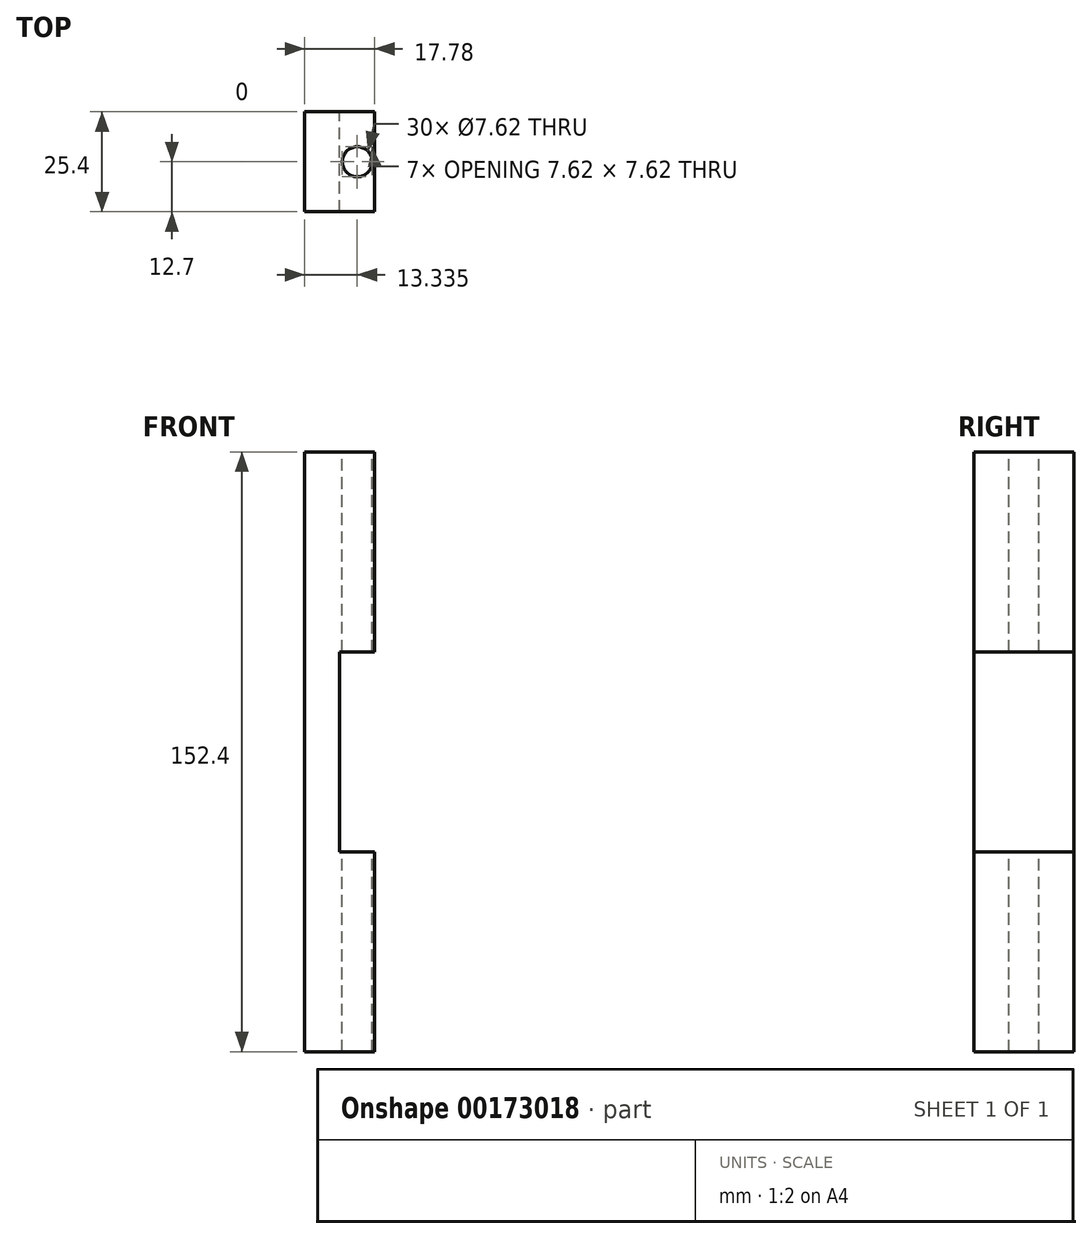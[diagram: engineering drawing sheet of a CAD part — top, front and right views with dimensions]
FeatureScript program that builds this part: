
annotation { "Feature Type Name" : "Feature", "Feature Type Description" : "" }
export const myFeature = defineFeature(function(context is Context, id is Id, definition is map)
    precondition{}
    {
        {
            var Q0;
            Q0=qCreatedBy(makeId("Front.planeOp"),FACE);
            var sketch = newSketch(context, id + "F0", { "sketchPlane" : qUnion([Q0])});
            skLineSegment(sketch, "E0.bottom", {"start": v(8.89, -76.2) * mm, "end": v(-8.9, -76.2) * mm});
            skLineSegment(sketch, "E0.top", {"start": v(8.9, 76.2) * mm, "end": v(-8.89, 76.2) * mm});
            skLineSegment(sketch, "E0.right", {"start": v(-8.9, -76.2) * mm, "end": v(-8.89, 76.2) * mm});
            skPoint(sketch, "E0.middle", {"position": v(0, 0) * mm});
            skLineSegment(sketch, "E1", {"start": v(8.9, 76.2) * mm, "end": v(8.9, 25.4) * mm});
            skLineSegment(sketch, "E2", {"start": v(8.9, 25.4) * mm, "end": v(0, 25.4) * mm});
            skLineSegment(sketch, "E3", {"start": v(8.89, -76.2) * mm, "end": v(8.89, -25.4) * mm});
            skLineSegment(sketch, "E4", {"start": v(8.89, -25.4) * mm, "end": v(0, -25.4) * mm});
            skLineSegment(sketch, "E5", {"start": v(0, -25.4) * mm, "end": v(0, 25.4) * mm});
            skSolve(sketch);
        }
        {
            var Q0;
            Q0=makeQuery(id+"F0.imprint","IMPRINT",FACE,{"disambiguationData":[TD([[makeQuery(id+"F0.imprint","IMPRINT",EDGE,{"derivedFrom":sQuery(id+"F0.wireOp",EDGE,"E0.bottom")}),-1.0]])]});
            extrude(context, id + "F1", {"entities" : qUnion([Q0]), "depth" : 25.4 * mm});
        }
        {
            var Q0;
            Q0=makeQuery(id+"F1.opExtrude","SWEPT_FACE",FACE,{"disambiguationData":[OSD([sQuery(id+"F0.wireOp",EDGE,"E0.top")])]});
            var sketch = newSketch(context, id + "F2", { "sketchPlane" : qUnion([Q0])});
            skLineSegment(sketch, "E6", {"start": v(0, 0) * mm, "end": v(4.45, 0) * mm});
            skLineSegment(sketch, "E7", {"start": v(4.45, 0) * mm, "end": v(4.45, -12.7) * mm});
            skCircle(sketch, "E8", {"center": v(4.45, -12.7) * mm, "radius": 3.81 * mm});
            skSolve(sketch);
        }
        {
            var Q0;
            Q0 = qSketchRegion(id + "F2", true);
            extrude(context, id + "F3", {"entities" : qUnion([Q0]), "operationType" : NewBodyOperationType.REMOVE, "endBound" : BoundingType.THROUGH_ALL, "oppositeDirection" : true, "depth" : 25.4 * mm});
        }
    });
